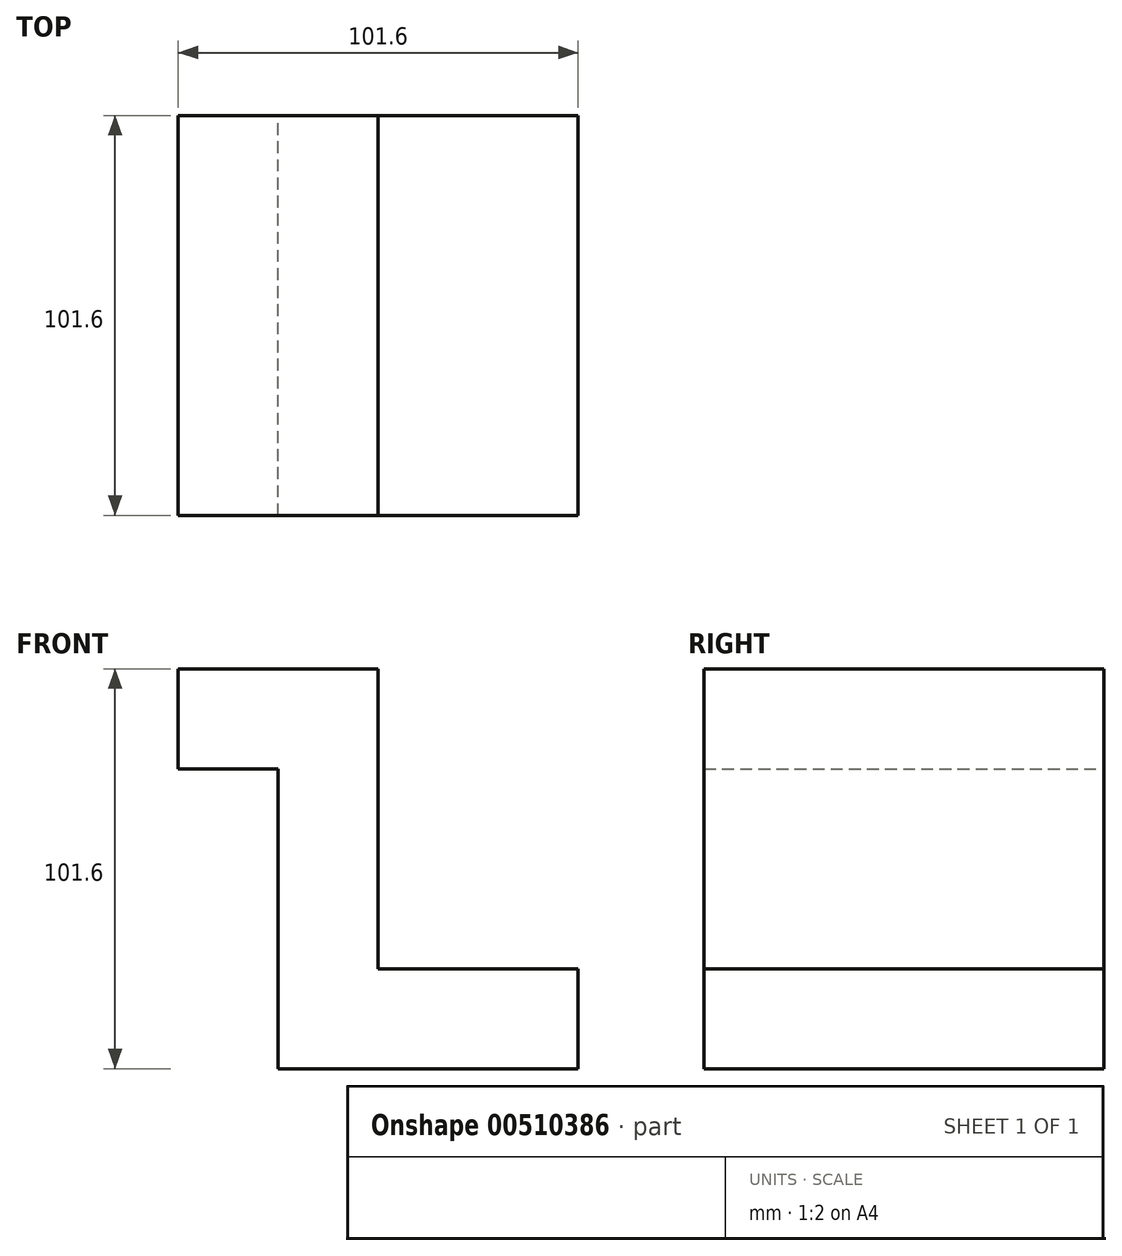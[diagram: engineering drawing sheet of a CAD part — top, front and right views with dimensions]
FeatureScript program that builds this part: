
annotation { "Feature Type Name" : "Feature", "Feature Type Description" : "" }
export const myFeature = defineFeature(function(context is Context, id is Id, definition is map)
    precondition{}
    {
        {
            var Q0;
            Q0=qCreatedBy(makeId("Front.planeOp"),FACE);
            var sketch = newSketch(context, id + "F0", { "sketchPlane" : qUnion([Q0])});
            skLineSegment(sketch, "E0", {"start": v(-101.6, 54.9) * mm, "end": v(-50.8, 54.9) * mm});
            skLineSegment(sketch, "E1", {"start": v(-101.6, 54.9) * mm, "end": v(-101.6, 29.5) * mm});
            skLineSegment(sketch, "E2", {"start": v(-101.6, 29.5) * mm, "end": v(-76.2, 29.5) * mm});
            skLineSegment(sketch, "E3", {"start": v(-76.2, 29.5) * mm, "end": v(-76.2, -46.7) * mm});
            skLineSegment(sketch, "E4", {"start": v(-76.2, -46.7) * mm, "end": v(0, -46.7) * mm});
            skLineSegment(sketch, "E5", {"start": v(0, -46.7) * mm, "end": v(0, -21.3) * mm});
            skLineSegment(sketch, "E6", {"start": v(0, -21.3) * mm, "end": v(-50.8, -21.3) * mm});
            skLineSegment(sketch, "E7", {"start": v(-50.8, -21.3) * mm, "end": v(-50.8, 54.9) * mm});
            skSolve(sketch);
        }
        {
            var Q0;
            Q0=makeQuery(id+"F0.imprint","IMPRINT",FACE,{"disambiguationData":[TD([[makeQuery(id+"F0.imprint","IMPRINT",EDGE,{"derivedFrom":sQuery(id+"F0.wireOp",EDGE,"E0")}),-1.0]])]});
            extrude(context, id + "F1", {"entities" : qUnion([Q0]), "depth" : 101.6 * mm});
        }
        {
            var Q0;
            Q0=makeQuery(id+"F1.opExtrude","SWEPT_FACE",FACE,{"disambiguationData":[OSD([sQuery(id+"F0.wireOp",EDGE,"E6")])]});
            var sketch = newSketch(context, id + "F2", { "sketchPlane" : qUnion([Q0])});
            skLineSegment(sketch, "E8.bottom", {"start": v(-37.21, -70.38) * mm, "end": v(-13.1, -70.38) * mm});
            skLineSegment(sketch, "E8.top", {"start": v(-37.21, -28.66) * mm, "end": v(-13.1, -28.66) * mm});
            skLineSegment(sketch, "E8.left", {"start": v(-37.21, -70.38) * mm, "end": v(-37.21, -28.66) * mm});
            skLineSegment(sketch, "E8.right", {"start": v(-13.1, -70.38) * mm, "end": v(-13.1, -28.66) * mm});
            skSolve(sketch);
        }
        {
            var Q0;
            Q0 = qSketchRegion(id + "F2", true);
            extrude(context, id + "F3", {"entities" : qUnion([Q0]), "operationType" : NewBodyOperationType.REMOVE, "oppositeDirection" : true, "depth" : 25.4 * mm});
        }
        {
            var Q0;
            Q0=makeQuery(id+"F3.boolean.opBoolean","COPY",FACE,{"derivedFrom":makeQuery(id+"F3.opExtrude","SWEPT_FACE",FACE,{"disambiguationData":[OSD([sQuery(id+"F2.wireOp",EDGE,"E8.left")])]})});
            extrude(context, id + "F4", {"entities" : qUnion([Q0]), "operationType" : NewBodyOperationType.ADD, "depth" : 25.4 * mm});
        }
        {
            var Q0;
            Q0=makeQuery(id+"F1.opExtrude","SWEPT_FACE",FACE,{"disambiguationData":[OSD([sQuery(id+"F0.wireOp",EDGE,"E5")])]});
            var sketch = newSketch(context, id + "F5", { "sketchPlane" : qUnion([Q0])});
            skLineSegment(sketch, "E9.bottom", {"start": v(-25.4, -30.16) * mm, "end": v(-56.33, -30.16) * mm});
            skLineSegment(sketch, "E9.top", {"start": v(-25.4, -36.9) * mm, "end": v(-56.33, -36.9) * mm});
            skLineSegment(sketch, "E9.left", {"start": v(-25.4, -30.16) * mm, "end": v(-25.4, -36.9) * mm});
            skLineSegment(sketch, "E9.right", {"start": v(-56.33, -30.16) * mm, "end": v(-56.33, -36.9) * mm});
            skSolve(sketch);
        }
        {
            var Q0;
            Q0 = qSketchRegion(id + "F5", true);
            extrude(context, id + "F6", {"entities" : qUnion([Q0]), "operationType" : NewBodyOperationType.REMOVE, "oppositeDirection" : true, "depth" : 25.4 * mm});
        }
        {
            var Q0;
            Q0=makeQuery(id+"F6.boolean.opBoolean","COPY",FACE,{"derivedFrom":makeQuery(id+"F6.opExtrude","CAP_FACE",FACE,{"disambiguationData":[OSD([sQuery(id+"F5.wireOp",EDGE,"E9.bottom"),sQuery(id+"F5.wireOp",EDGE,"E9.top"),sQuery(id+"F5.wireOp",EDGE,"E9.left"),sQuery(id+"F5.wireOp",EDGE,"E9.right")])],"isStart":false})});
            extrude(context, id + "F7", {"entities" : qUnion([Q0]), "operationType" : NewBodyOperationType.ADD, "depth" : 25.4 * mm});
        }
    });
